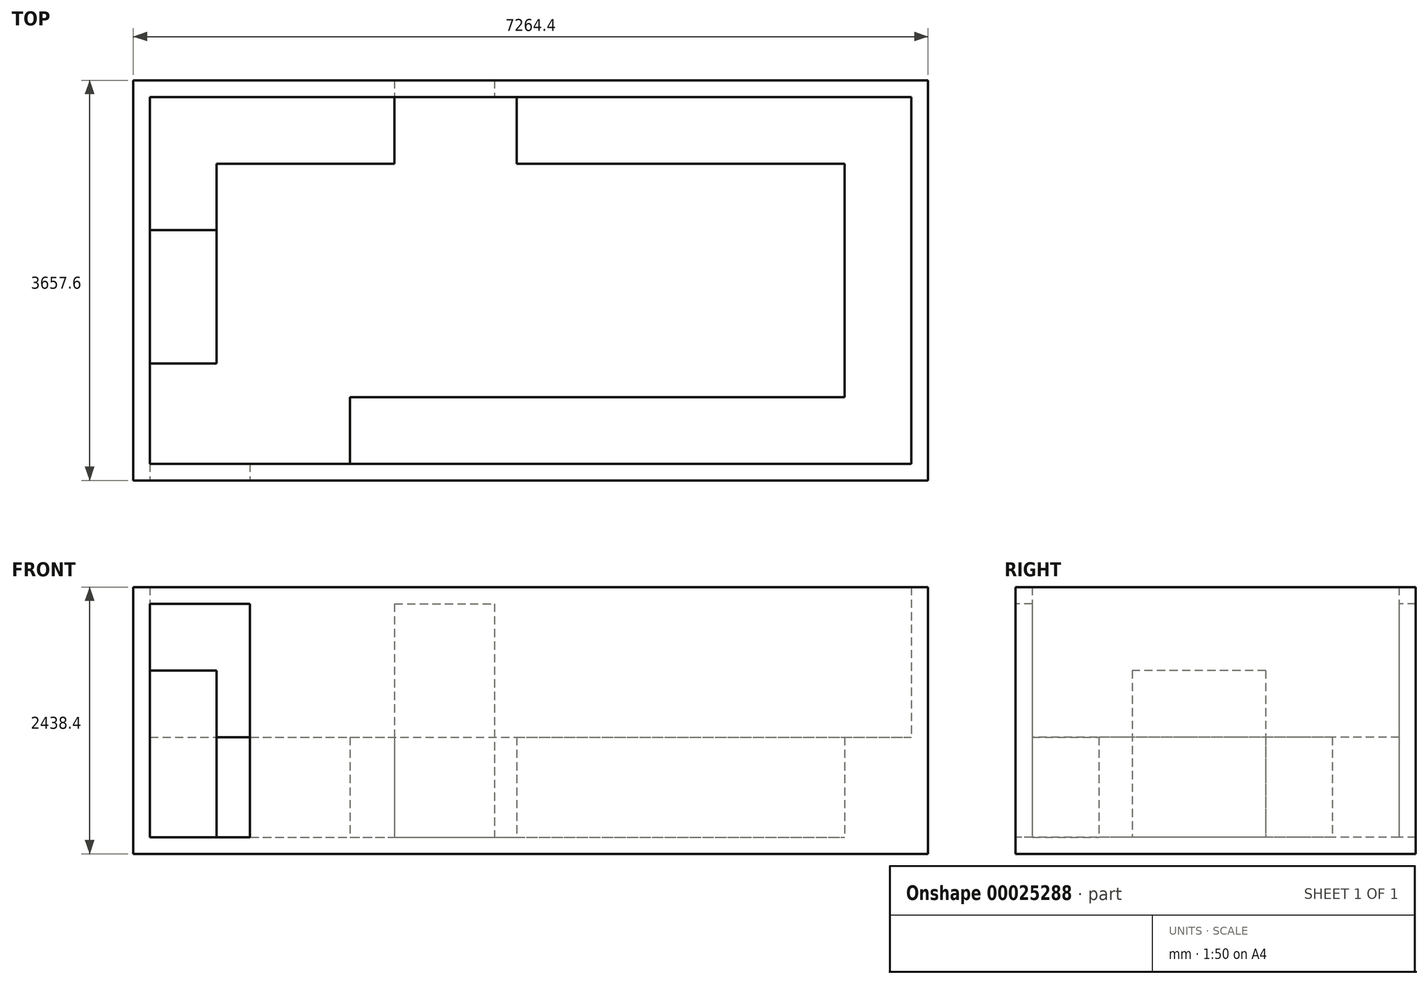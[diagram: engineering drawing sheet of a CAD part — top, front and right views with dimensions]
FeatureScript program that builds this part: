
annotation { "Feature Type Name" : "Feature", "Feature Type Description" : "" }
export const myFeature = defineFeature(function(context is Context, id is Id, definition is map)
    precondition{}
    {
        {
            var Q0;
            Q0=qCreatedBy(makeId("Top.planeOp"),FACE);
            var sketch = newSketch(context, id + "F0", { "sketchPlane" : qUnion([Q0])});
            skLineSegment(sketch, "E0.bottom", {"start": v(-3627.44, 1739.05) * mm, "end": v(3636.96, 1739.05) * mm});
            skLineSegment(sketch, "E0.top", {"start": v(-3627.44, -1918.55) * mm, "end": v(3636.96, -1918.55) * mm});
            skLineSegment(sketch, "E0.left", {"start": v(-3627.44, 1739.05) * mm, "end": v(-3627.44, -1918.55) * mm});
            skLineSegment(sketch, "E0.right", {"start": v(3636.96, 1739.05) * mm, "end": v(3636.96, -1918.55) * mm});
            skSolve(sketch);
        }
        {
            var Q0;
            Q0 = qSketchRegion(id + "F0", true);
            extrude(context, id + "F1", {"entities" : qUnion([Q0]), "depth" : 2438.4 * mm});
        }
        {
            var Q0;
            Q0=makeQuery(id+"F1.opExtrude","CAP_FACE",FACE,{"disambiguationData":[OSD([sQuery(id+"F0.wireOp",EDGE,"E0.bottom"),sQuery(id+"F0.wireOp",EDGE,"E0.top"),sQuery(id+"F0.wireOp",EDGE,"E0.left"),sQuery(id+"F0.wireOp",EDGE,"E0.right")])],"isStart":false});
            shell(context, id + "F2", {"entities" : qUnion([Q0]), "thickness" : 152.4 * mm});
        }
        {
            var Q0;
            Q0=makeQuery(id+"F1.opExtrude","SWEPT_FACE",FACE,{"disambiguationData":[OSD([sQuery(id+"F0.wireOp",EDGE,"E0.top")])]});
            var sketch = newSketch(context, id + "F3", { "sketchPlane" : qUnion([Q0])});
            skLineSegment(sketch, "E1.bottom", {"start": v(-3475.04, 2286) * mm, "end": v(-2560.64, 2286) * mm});
            skLineSegment(sketch, "E1.top", {"start": v(-3475.04, 152.4) * mm, "end": v(-2560.64, 152.4) * mm});
            skLineSegment(sketch, "E1.left", {"start": v(-3475.04, 2286) * mm, "end": v(-3475.04, 152.4) * mm});
            skLineSegment(sketch, "E1.right", {"start": v(-2560.64, 2286) * mm, "end": v(-2560.64, 152.4) * mm});
            skSolve(sketch);
        }
        {
            var Q0;
            Q0=makeQuery(id+"F3.imprint","IMPRINT",FACE,{"disambiguationData":[TD([[makeQuery(id+"F3.imprint","IMPRINT",EDGE,{"derivedFrom":sQuery(id+"F3.wireOp",EDGE,"E1.bottom")}),-1.0]])]});
            extrude(context, id + "F4", {"entities" : qUnion([Q0]), "operationType" : NewBodyOperationType.REMOVE, "oppositeDirection" : true, "depth" : 152.4 * mm});
        }
        {
            var Q0;
            Q0=qCreatedBy(makeId("Top.planeOp"),FACE);
            var sketch = newSketch(context, id + "F5", { "sketchPlane" : qUnion([Q0])});
            skLineSegment(sketch, "E2.bottom", {"start": v(-3475.04, 1586.65) * mm, "end": v(-2865.44, 1586.65) * mm});
            skLineSegment(sketch, "E2.top", {"start": v(-3475.04, 367.45) * mm, "end": v(-2865.44, 367.45) * mm});
            skLineSegment(sketch, "E2.left", {"start": v(-3475.04, 1586.65) * mm, "end": v(-3475.04, 367.45) * mm});
            skLineSegment(sketch, "E2.right", {"start": v(-2865.44, 1586.65) * mm, "end": v(-2865.44, 367.45) * mm});
            skSolve(sketch);
        }
        {
            var Q0;
            Q0=makeQuery(id+"F4.boolean.opBoolean","MERGE",FACE,{"derivedFrom":[makeQuery(id+"F2.opShell","OFFSET_FACE",FACE,{"disambiguationData":[OSD([sQuery(id+"F0.wireOp",EDGE,"E0.bottom"),sQuery(id+"F0.wireOp",EDGE,"E0.top"),sQuery(id+"F0.wireOp",EDGE,"E0.left"),sQuery(id+"F0.wireOp",EDGE,"E0.right")])]}),makeQuery(id+"F4.opExtrude","SWEPT_FACE",FACE,{"disambiguationData":[OSD([sQuery(id+"F3.wireOp",EDGE,"E1.top")])]})]});
            var sketch = newSketch(context, id + "F6", { "sketchPlane" : qUnion([Q0])});
            skLineSegment(sketch, "E3.bottom", {"start": v(-1646.24, -1766.15) * mm, "end": v(-122.24, -1766.15) * mm});
            skLineSegment(sketch, "E3.top", {"start": v(-1646.24, -1156.55) * mm, "end": v(-122.24, -1156.55) * mm});
            skLineSegment(sketch, "E3.left", {"start": v(-1646.24, -1766.15) * mm, "end": v(-1646.24, -1156.55) * mm});
            skLineSegment(sketch, "E3.right", {"start": v(-122.24, -1766.15) * mm, "end": v(-122.24, -1156.55) * mm});
            skSolve(sketch);
        }
        {
            var Q0;
            Q0=makeQuery(id+"F6.imprint","IMPRINT",FACE,{"disambiguationData":[TD([[makeQuery(id+"F6.imprint","IMPRINT",EDGE,{"derivedFrom":sQuery(id+"F6.wireOp",EDGE,"E3.bottom")}),1.0]])]});
            extrude(context, id + "F7", {"entities" : qUnion([Q0]), "operationType" : NewBodyOperationType.ADD, "depth" : 914.4 * mm});
        }
        {
            var Q0;
            Q0=makeQuery(id+"F4.boolean.opBoolean","MERGE",FACE,{"derivedFrom":[makeQuery(id+"F2.opShell","OFFSET_FACE",FACE,{"disambiguationData":[OSD([sQuery(id+"F0.wireOp",EDGE,"E0.bottom"),sQuery(id+"F0.wireOp",EDGE,"E0.top"),sQuery(id+"F0.wireOp",EDGE,"E0.left"),sQuery(id+"F0.wireOp",EDGE,"E0.right")])]}),makeQuery(id+"F4.opExtrude","SWEPT_FACE",FACE,{"disambiguationData":[OSD([sQuery(id+"F3.wireOp",EDGE,"E1.top")])]})]});
            var sketch = newSketch(context, id + "F8", { "sketchPlane" : qUnion([Q0])});
            skLineSegment(sketch, "E4.bottom", {"start": v(3484.56, 1586.65) * mm, "end": v(-122.24, 1586.65) * mm});
            skLineSegment(sketch, "E4.top", {"start": v(3484.56, -1766.15) * mm, "end": v(-122.24, -1766.15) * mm});
            skLineSegment(sketch, "E4.left", {"start": v(3484.56, 1586.65) * mm, "end": v(3484.56, -1766.15) * mm});
            skLineSegment(sketch, "E5.bottom", {"start": v(-122.24, 977.05) * mm, "end": v(2874.96, 977.05) * mm});
            skLineSegment(sketch, "E5.top", {"start": v(-122.24, -1156.55) * mm, "end": v(2874.96, -1156.55) * mm});
            skLineSegment(sketch, "E5.right", {"start": v(2874.96, 977.05) * mm, "end": v(2874.96, -1156.55) * mm});
            skLineSegment(sketch, "E6", {"start": v(-122.24, 977.05) * mm, "end": v(-122.24, 1586.65) * mm});
            skLineSegment(sketch, "E7", {"start": v(-122.24, -1156.55) * mm, "end": v(-122.24, -1766.15) * mm});
            skLineSegment(sketch, "E8", {"start": v(2874.96, 977.05) * mm, "end": v(-122.24, 977.05) * mm});
            skSolve(sketch);
        }
        {
            var Q0;
            Q0=makeQuery(id+"F8.imprint","IMPRINT",FACE,{"disambiguationData":[TD([[makeQuery(id+"F8.imprint","IMPRINT",EDGE,{"derivedFrom":sQuery(id+"F8.wireOp",EDGE,"E4.bottom")}),-1.0]])]});
            extrude(context, id + "F9", {"entities" : qUnion([Q0]), "operationType" : NewBodyOperationType.ADD, "depth" : 914.4 * mm});
        }
        {
            var Q0;
            Q0=makeQuery(id+"F2.opShell","OFFSET_FACE",FACE,{"disambiguationData":[OSD([sQuery(id+"F0.wireOp",EDGE,"E0.bottom")])]});
            var sketch = newSketch(context, id + "F10", { "sketchPlane" : qUnion([Q0])});
            skLineSegment(sketch, "E9.bottom", {"start": v(-1239.84, 2286) * mm, "end": v(-325.44, 2286) * mm});
            skLineSegment(sketch, "E9.top", {"start": v(-1239.84, 152.4) * mm, "end": v(-325.44, 152.4) * mm});
            skLineSegment(sketch, "E9.left", {"start": v(-1239.84, 2286) * mm, "end": v(-1239.84, 152.4) * mm});
            skLineSegment(sketch, "E9.right", {"start": v(-325.44, 2286) * mm, "end": v(-325.44, 152.4) * mm});
            skSolve(sketch);
        }
        {
            var Q0;
            Q0 = qSketchRegion(id + "F10", true);
            extrude(context, id + "F11", {"entities" : qUnion([Q0]), "operationType" : NewBodyOperationType.REMOVE, "oppositeDirection" : true, "depth" : 152.4 * mm});
        }
        {
            var Q0;
            Q0=makeQuery(id+"F11.boolean.opBoolean","MERGE",FACE,{"derivedFrom":[makeQuery(id+"F4.boolean.opBoolean","MERGE",FACE,{"derivedFrom":[makeQuery(id+"F2.opShell","OFFSET_FACE",FACE,{"disambiguationData":[OSD([sQuery(id+"F0.wireOp",EDGE,"E0.bottom"),sQuery(id+"F0.wireOp",EDGE,"E0.top"),sQuery(id+"F0.wireOp",EDGE,"E0.left"),sQuery(id+"F0.wireOp",EDGE,"E0.right")])]}),makeQuery(id+"F4.opExtrude","SWEPT_FACE",FACE,{"disambiguationData":[OSD([sQuery(id+"F3.wireOp",EDGE,"E1.top")])]})]}),makeQuery(id+"F11.opExtrude","SWEPT_FACE",FACE,{"disambiguationData":[OSD([sQuery(id+"F10.wireOp",EDGE,"E9.top")])]})]});
            var sketch = newSketch(context, id + "F12", { "sketchPlane" : qUnion([Q0])});
            skLineSegment(sketch, "E10.bottom", {"start": v(-3475.04, 367.67) * mm, "end": v(-2865.44, 367.67) * mm});
            skLineSegment(sketch, "E10.top", {"start": v(-3475.04, -851.53) * mm, "end": v(-2865.44, -851.53) * mm});
            skLineSegment(sketch, "E10.left", {"start": v(-3475.04, 367.67) * mm, "end": v(-3475.04, -851.53) * mm});
            skLineSegment(sketch, "E10.right", {"start": v(-2865.44, 367.67) * mm, "end": v(-2865.44, -851.53) * mm});
            skSolve(sketch);
        }
        {
            var Q0;
            Q0=makeQuery(id+"F12.imprint","IMPRINT",FACE,{"disambiguationData":[TD([[makeQuery(id+"F12.imprint","IMPRINT",EDGE,{"derivedFrom":sQuery(id+"F12.wireOp",EDGE,"E10.bottom")}),-1.0]])]});
            extrude(context, id + "F13", {"entities" : qUnion([Q0]), "depth" : 1524 * mm});
        }
        {
            var Q0;
            Q0=makeQuery(id+"F11.boolean.opBoolean","MERGE",FACE,{"derivedFrom":[makeQuery(id+"F4.boolean.opBoolean","MERGE",FACE,{"derivedFrom":[makeQuery(id+"F2.opShell","OFFSET_FACE",FACE,{"disambiguationData":[OSD([sQuery(id+"F0.wireOp",EDGE,"E0.bottom"),sQuery(id+"F0.wireOp",EDGE,"E0.top"),sQuery(id+"F0.wireOp",EDGE,"E0.left"),sQuery(id+"F0.wireOp",EDGE,"E0.right")])]}),makeQuery(id+"F4.opExtrude","SWEPT_FACE",FACE,{"disambiguationData":[OSD([sQuery(id+"F3.wireOp",EDGE,"E1.top")])]})]}),makeQuery(id+"F11.opExtrude","SWEPT_FACE",FACE,{"disambiguationData":[OSD([sQuery(id+"F10.wireOp",EDGE,"E9.top")])]})]});
            var sketch = newSketch(context, id + "F14", { "sketchPlane" : qUnion([Q0])});
            skLineSegment(sketch, "E11.bottom", {"start": v(-3475.04, 1586.65) * mm, "end": v(-1239.84, 1586.65) * mm});
            skLineSegment(sketch, "E11.top", {"start": v(-3475.04, 977.05) * mm, "end": v(-1239.84, 977.05) * mm});
            skLineSegment(sketch, "E11.left", {"start": v(-3475.04, 1586.65) * mm, "end": v(-3475.04, 977.05) * mm});
            skLineSegment(sketch, "E11.right", {"start": v(-1239.84, 1586.65) * mm, "end": v(-1239.84, 977.05) * mm});
            skLineSegment(sketch, "E12.top", {"start": v(-3475.04, 367.45) * mm, "end": v(-2865.44, 367.45) * mm});
            skLineSegment(sketch, "E12.left", {"start": v(-3475.04, 977.05) * mm, "end": v(-3475.04, 367.45) * mm});
            skLineSegment(sketch, "E12.right", {"start": v(-2865.44, 977.05) * mm, "end": v(-2865.44, 367.45) * mm});
            skSolve(sketch);
        }
        {
            var Q0;
            Q0=makeQuery(id+"F14.imprint","IMPRINT",FACE,{"disambiguationData":[TD([[makeQuery(id+"F14.imprint","IMPRINT",EDGE,{"derivedFrom":sQuery(id+"F14.wireOp",EDGE,"E12.top")}),1.0]])]});
            var Q1;
            Q1=makeQuery(id+"F14.imprint","IMPRINT",FACE,{"disambiguationData":[TD([[makeQuery(id+"F14.imprint","IMPRINT",EDGE,{"derivedFrom":sQuery(id+"F14.wireOp",EDGE,"E11.bottom")}),-1.0]])]});
            extrude(context, id + "F15", {"entities" : qUnion([Q0, Q1]), "depth" : 914.4 * mm});
        }
    });
